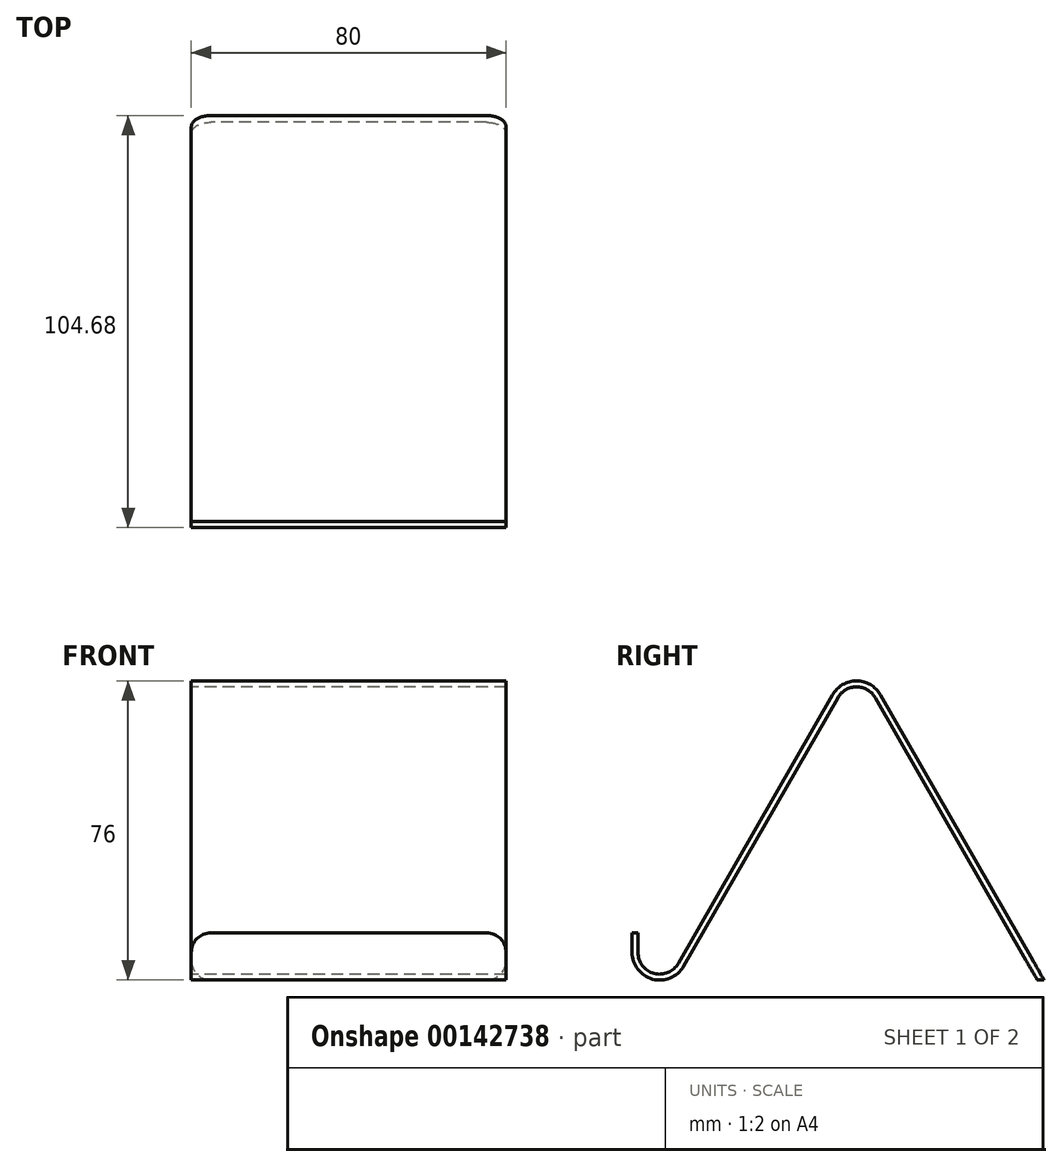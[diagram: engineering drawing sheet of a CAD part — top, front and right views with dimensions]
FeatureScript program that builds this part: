
annotation { "Feature Type Name" : "Feature", "Feature Type Description" : "" }
export const myFeature = defineFeature(function(context is Context, id is Id, definition is map)
    precondition{}
    {
        {
            var Q0;
            Q0=qCreatedBy(makeId("Right.planeOp"),FACE);
            var sketch = newSketch(context, id + "F0", { "sketchPlane" : qUnion([Q0])});
            skArc(sketch, "E0", {"start": v(-7, 0) * mm, "mid": v(-1.8, -6.76) * mm, "end": v(6.07, -3.48) * mm});
            skArc(sketch, "E1", {"start": v(54.77, 64.74) * mm, "mid": v(50, 67.5) * mm, "end": v(45.23, 64.74) * mm});
            skLineSegment(sketch, "E2", {"start": v(6.07, -3.48) * mm, "end": v(45.23, 64.74) * mm});
            skLineSegment(sketch, "E3", {"start": v(50, 62) * mm, "end": v(50, 0) * mm, "construction": true});
            skLineSegment(sketch, "E4.MirrorCS", {"start": v(95.95, -7) * mm, "end": v(54.77, 64.74) * mm});
            skLineSegment(sketch, "E5", {"start": v(0, -7) * mm, "end": v(110.77, -7) * mm, "construction": true});
            skLineSegment(sketch, "E6", {"start": v(-7, 0) * mm, "end": v(-7, 5) * mm});
            skLineSegment(sketch, "E7.0", {"start": v(-5.5, 0) * mm, "end": v(-5.5, 5) * mm});
            skLineSegment(sketch, "E7.1", {"start": v(97.68, -7) * mm, "end": v(56.07, 65.48) * mm});
            skArc(sketch, "E7.2", {"start": v(56.07, 65.48) * mm, "mid": v(50, 69) * mm, "end": v(43.93, 65.48) * mm});
            skLineSegment(sketch, "E7.3", {"start": v(4.77, -2.74) * mm, "end": v(43.93, 65.48) * mm});
            skArc(sketch, "E7.4", {"start": v(-5.5, 0) * mm, "mid": v(-1.42, -5.31) * mm, "end": v(4.77, -2.74) * mm});
            skLineSegment(sketch, "E8", {"start": v(-7, 5) * mm, "end": v(-5.5, 5) * mm});
            skLineSegment(sketch, "E9", {"start": v(95.95, -7) * mm, "end": v(97.68, -7) * mm});
            skSolve(sketch);
        }
        {
            var Q0;
            Q0 = qSketchRegion(id + "F0", true);
            extrude(context, id + "F1", {"entities" : qUnion([Q0]), "endBound" : BoundingType.SYMMETRIC, "depth" : 80 * mm});
        }
        {
            var Q0;
            Q0=makeQuery(id+"F1.opExtrude","CAP_EDGE",EDGE,{"disambiguationData":[OSD([sQuery(id+"F0.wireOp",EDGE,"E8")])],"isStart":false});
            var Q1;
            Q1=makeQuery(id+"F1.opExtrude","CAP_EDGE",EDGE,{"disambiguationData":[OSD([sQuery(id+"F0.wireOp",EDGE,"E8")])],"isStart":true});
            var Q2;
            Q2=makeQuery(id+"F1.opExtrude","CAP_EDGE",EDGE,{"disambiguationData":[OSD([sQuery(id+"F0.wireOp",EDGE,"E9")])],"isStart":false});
            var Q3;
            Q3=makeQuery(id+"F1.opExtrude","CAP_EDGE",EDGE,{"disambiguationData":[OSD([sQuery(id+"F0.wireOp",EDGE,"E9")])],"isStart":true});
            fillet(context, id + "F2", {"entities" : qUnion([Q0, Q1, Q2, Q3]), "radius" : 5 * mm, "tangentPropagation" : true, "allowEdgeOverflow" : false});
        }
    });
